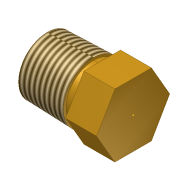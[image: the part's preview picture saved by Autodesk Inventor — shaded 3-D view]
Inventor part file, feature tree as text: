
AUTODESK INVENTOR PART (.ipt)
format: ipt  version: Autodesk Inventor 10  size: 172,032 bytes
history: native  units: mm (DEFAULTED — no unit token found)
features: thread x2, sketch x1, imported_body x1
ambient origin geometry x8: Origin, YZ Plane, XZ Plane, XY Plane, X Axis, Y Axis, Z Axis, Center Point
feature tree (4):
  sketch  "Sketch1"
  imported_body  "Base1"
  thread  "Thread1"  [1 undecoded]
  thread  "Thread2"  [1 undecoded]
note: 2 required parameter values undecoded (feature->parameter linkage not recoverable at this tier; creation-order binding heuristic only, values carry confidence <= 0.55)
